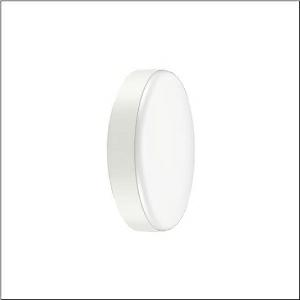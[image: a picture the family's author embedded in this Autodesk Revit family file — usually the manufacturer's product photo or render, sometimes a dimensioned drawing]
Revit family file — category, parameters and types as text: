
# Revit family: rondel_31_51wc10mb34as
name_source: partatom
category: Lighting Fixtures
units: mm (PartAtom-declared; Revit-internal decimal feet)

## family parameters
Cut with Voids When Loaded = No
Host = Face
Light Source = No
Part Type = Normal
Room Calculation Point = No
Round Connector Dimension = Use Diameter
Shared = No

## types (1)
- --- (1 x LED, 4250 lm, 35.4 W, 3000K)
    Apparent Load = 35 VA
    CIE Flux Codes = 44 75 94 94 100
    Color Rendering = 80
    Color Temperature = 3000K
    Default Elevation = 1800 mm
    Description = Rondel 31, wall and ceiling luminaire, primary optical cover: cover, of PC, opal, light emission: direct distribution, primary light characteristic: symmetric, installation type: surface-mounted, LED, rated luminous flux: 4.100lm, luminous efficacy: 112lm/W, light colour: 830, colour temperature: 3000K, with terminal, 3-pole, max. 2.5mm², mains connection: 220..240V, AC, 50/60Hz, rated input power: 35W, luminaire housing, of PC, traffic white (RAL 9016), diameter: 480mm, brightness and presence sensor, HF sensor, protection rating (complete): IP65, insulation class (complete): insulation class II (safety insulation), certification: CE, impact resistance: IK10, permissible storage temperature: -20..+60°C, packaging unit: 1 piece
    Height = 97 mm
    Lamp = 1 x LED
    Lamp Light Flux = 4250 lm
    Lamp Power = 35.4 W
    Lamp count = 1
    Length = 480 mm
    Luminous efficacy = 120 lm/W
    Manufacturer = Siteco
    ModVariant = No
    Model = 51WC10MB34AS
    Mounting Place = Ceiling
    Mounting Type = Surface mounted
    Number of Poles = 1
    OnlyDefault = Yes
    Power Factor = 1
    Product Name = Rondel 31
    Product group = wall and ceiling luminaire
    ProductGroupID = 301
    Protection Class = Protection class II
    Protection Degree = IP 65
    RLX_Detail_Level = 1
    RlxData = <blob elided: 41389 chars, md5=70a6f693>
    Socket = socket
    Standby Power = 0 W
    System Light Flux = 4250 lm
    System Power = 35 W
    Type Comments = factory setting: luminous flux: 100 % | (ON | ON)
    Type Image = l_1007188.jpg
    URL = http://relux.com
    VarID = @adj_020221
    Voltage = 0 V
    Weight = 0.00 kg
    Width = 0 mm  [stored 0 ft]

note: [stored X ft] marks values corroborated as IEEE doubles in the binary element streams (Revit-internal decimal feet)

## geometry (parser evidence)
native form markers: Blend x4, Sweep x12
no freeform markers — native parametric forms only
